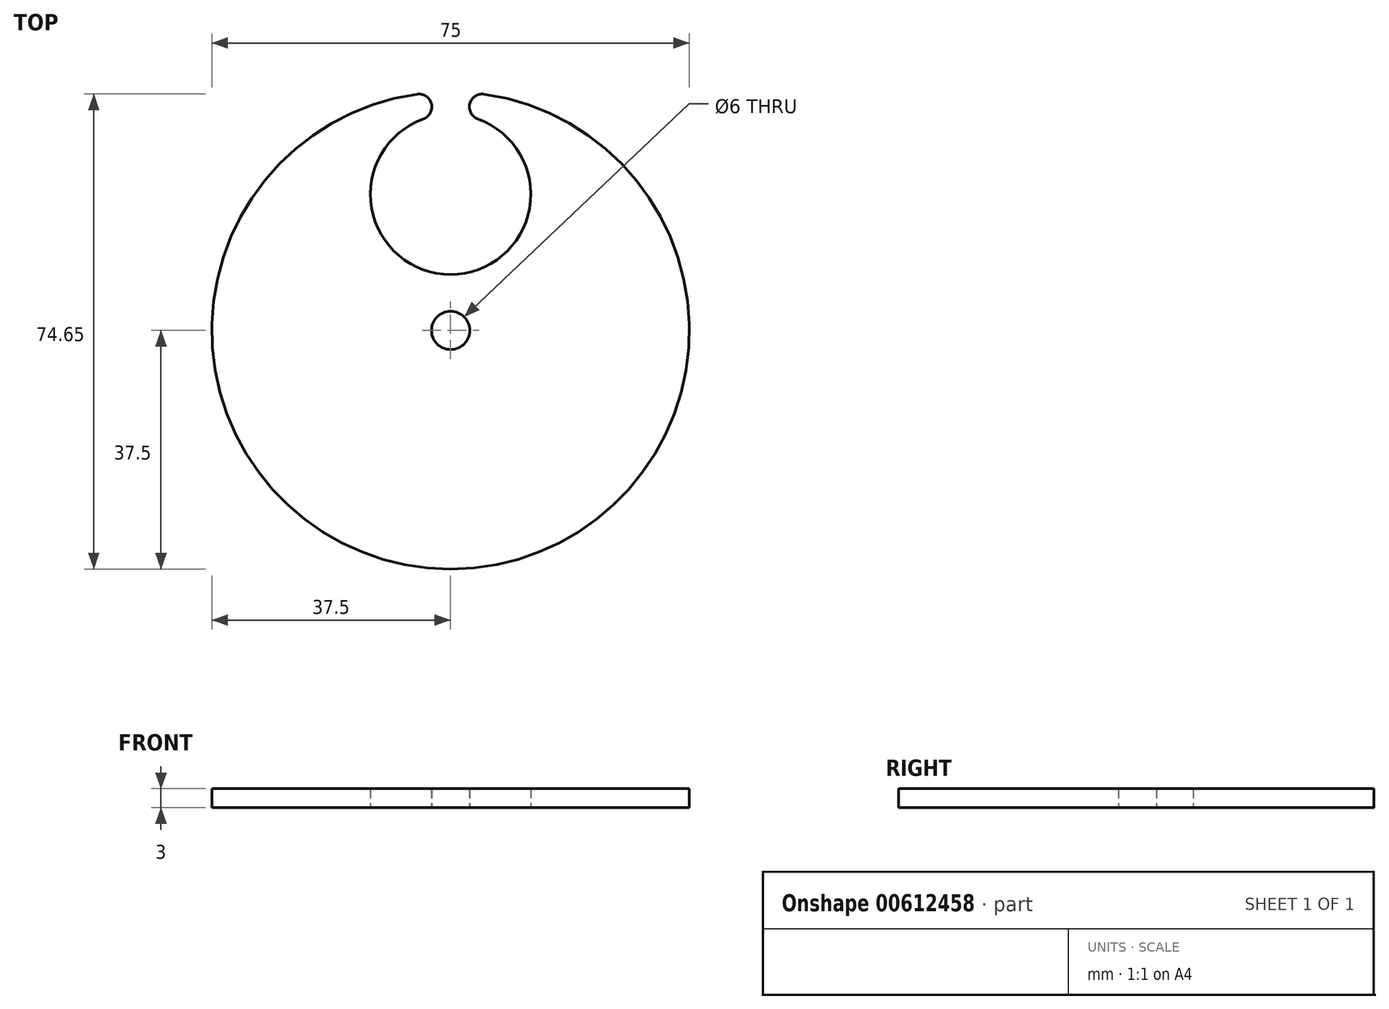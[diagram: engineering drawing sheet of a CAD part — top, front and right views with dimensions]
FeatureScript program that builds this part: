
annotation { "Feature Type Name" : "Feature", "Feature Type Description" : "" }
export const myFeature = defineFeature(function(context is Context, id is Id, definition is map)
    precondition{}
    {
        {
            var Q0;
            Q0=qCreatedBy(makeId("Top.planeOp"),FACE);
            var sketch = newSketch(context, id + "F0", { "sketchPlane" : qUnion([Q0])});
            skLineSegment(sketch, "E0.bottom", {"start": v(0, 0) * mm, "end": v(75, 0) * mm, "construction": true});
            skLineSegment(sketch, "E0.top", {"start": v(0, 75) * mm, "end": v(75, 75) * mm, "construction": true});
            skLineSegment(sketch, "E0.left", {"start": v(0, 0) * mm, "end": v(0, 75) * mm, "construction": true});
            skLineSegment(sketch, "E0.right", {"start": v(75, 0) * mm, "end": v(75, 75) * mm, "construction": true});
            skLineSegment(sketch, "E1", {"start": v(0, 75) * mm, "end": v(75, 0) * mm, "construction": true});
            skCircle(sketch, "E2", {"center": v(37.5, 37.5) * mm, "radius": 3 * mm});
            skCircle(sketch, "E3", {"center": v(37.5, 37.5) * mm, "radius": 37.5 * mm});
            skCircle(sketch, "E4", {"center": v(37.5, 58.88) * mm, "radius": 12.6 * mm});
            skArc(sketch, "E5", {"start": v(33.21, 70.72) * mm, "mid": v(34.49, 73.11) * mm, "end": v(32.24, 74.63) * mm});
            skArc(sketch, "E6", {"start": v(42.76, 74.63) * mm, "mid": v(40.51, 73.11) * mm, "end": v(41.79, 70.72) * mm});
            skSolve(sketch);
        }
        {
            var Q0;
            Q0=makeQuery(id+"F0.imprint","IMPRINT",FACE,{"disambiguationData":[TD([[makeQuery(id+"F0.imprint","IMPRINT",EDGE,{"derivedFrom":sQuery(id+"F0.wireOp",EDGE,"E2")}),-1.0]])]});
            extrude(context, id + "F1", {"entities" : qUnion([Q0]), "depth" : 3 * mm, "offsetDistance" : 25 * mm});
        }
    });
